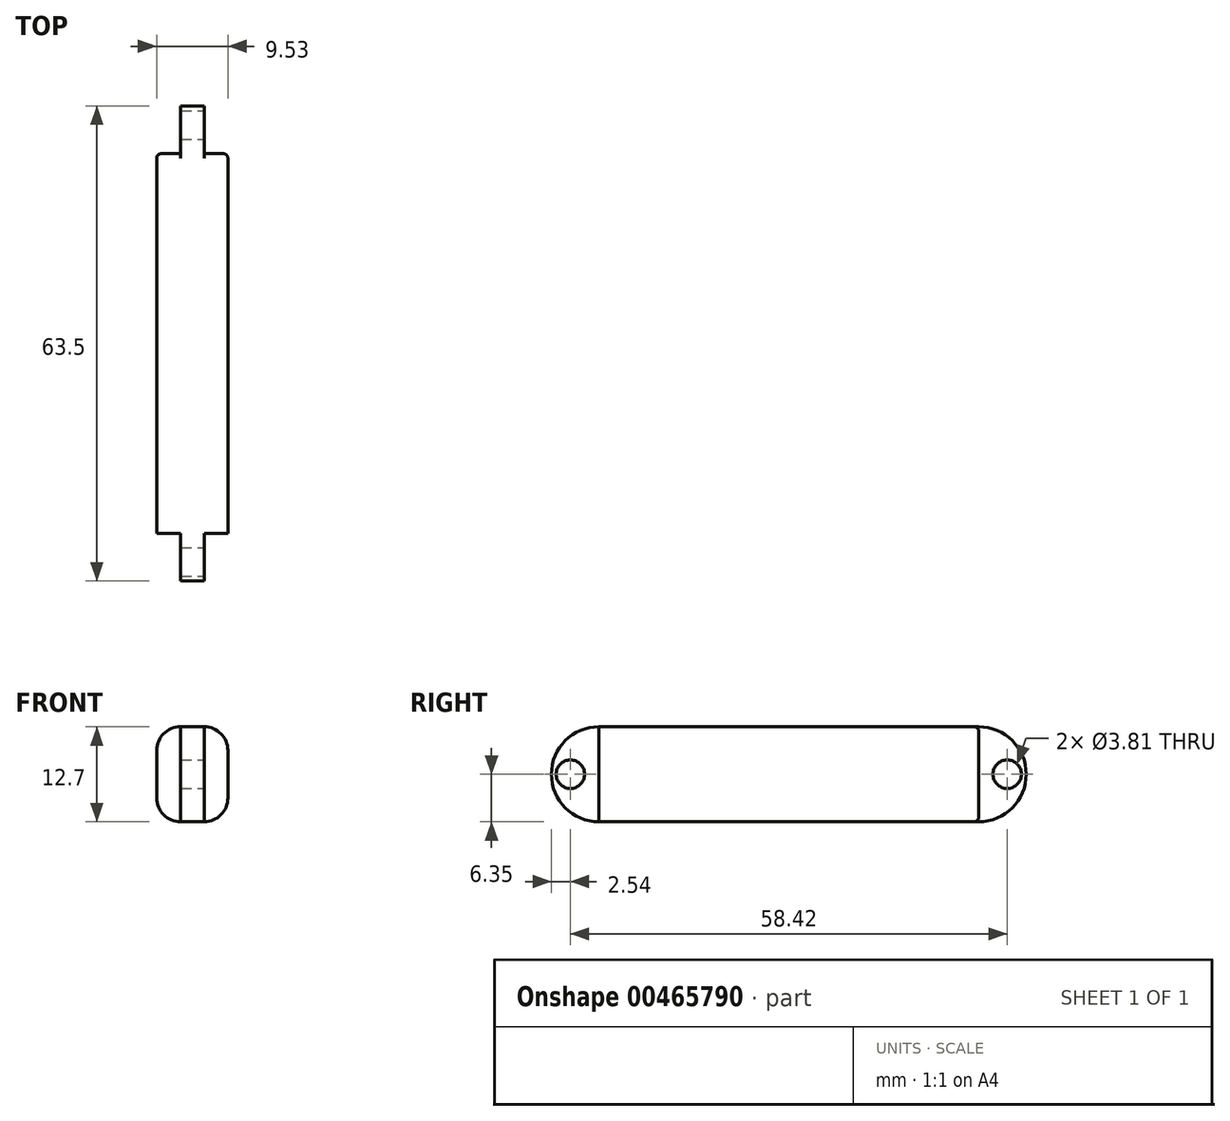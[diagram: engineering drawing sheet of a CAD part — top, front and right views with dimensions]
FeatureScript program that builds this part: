
annotation { "Feature Type Name" : "Feature", "Feature Type Description" : "" }
export const myFeature = defineFeature(function(context is Context, id is Id, definition is map)
    precondition{}
    {
        {
            var Q0;
            Q0=qCreatedBy(makeId("Right.planeOp"),FACE);
            var sketch = newSketch(context, id + "F0", { "sketchPlane" : qUnion([Q0])});
            skLineSegment(sketch, "E0.bottom", {"start": v(0, 0) * mm, "end": v(50.8, 0) * mm});
            skLineSegment(sketch, "E0.top", {"start": v(0, 12.7) * mm, "end": v(50.8, 12.7) * mm});
            skLineSegment(sketch, "E0.left", {"start": v(0, 0) * mm, "end": v(0, 12.7) * mm});
            skLineSegment(sketch, "E0.right", {"start": v(50.8, 0) * mm, "end": v(50.8, 12.7) * mm});
            skSolve(sketch);
        }
        {
            var Q0;
            Q0=qSketchRegion(id+"F0",true);
            extrude(context, id + "F1", {"entities" : qUnion([Q0]), "depth" : 9.52 * mm});
        }
        {
            var Q0;
            Q0=makeQuery(id+"F1.opExtrude","CAP_FACE",FACE,{"disambiguationData":[OSD([sQuery(id+"F0.wireOp",EDGE,"E0.bottom"),sQuery(id+"F0.wireOp",EDGE,"E0.top"),sQuery(id+"F0.wireOp",EDGE,"E0.left"),sQuery(id+"F0.wireOp",EDGE,"E0.right")])],"isStart":true});
            var sketch = newSketch(context, id + "F2", { "sketchPlane" : qUnion([Q0])});
            skArc(sketch, "E1", {"start": v(0, 12.7) * mm, "mid": v(6.35, 6.35) * mm, "end": v(0, 0) * mm});
            skArc(sketch, "E2", {"start": v(-50.8, 0) * mm, "mid": v(-57.15, 6.35) * mm, "end": v(-50.8, 12.7) * mm});
            skLineSegment(sketch, "E3", {"start": v(0, 0) * mm, "end": v(0, 12.7) * mm});
            skLineSegment(sketch, "E4", {"start": v(-50.8, 0) * mm, "end": v(-50.8, 12.7) * mm});
            skSolve(sketch);
        }
        {
            var Q0;
            Q0=qSketchRegion(id+"F2",true);
            var Q1;
            Q1=makeQuery(id+"F2.imprint","IMPRINT",FACE,{"disambiguationData":[TD([[makeQuery(id+"F2.imprint","IMPRINT",EDGE,{"derivedFrom":sQuery(id+"F2.wireOp",EDGE,"E2")}),-1.0]])]});
            var Q2;
            Q2=makeQuery(id+"F2.imprint","IMPRINT",FACE,{"disambiguationData":[TD([[makeQuery(id+"F2.imprint","IMPRINT",EDGE,{"derivedFrom":sQuery(id+"F2.wireOp",EDGE,"E1")}),-1.0]])]});
            extrude(context, id + "F3", {"entities" : qUnion([Q0, Q1, Q2]), "operationType" : NewBodyOperationType.ADD, "oppositeDirection" : true, "depth" : 9.52 * mm});
        }
        {
            var Q0;
            Q0=qSketchRegion(id+"F2",true);
            extrude(context, id + "F4", {"entities" : qUnion([Q0]), "operationType" : NewBodyOperationType.REMOVE, "oppositeDirection" : true, "depth" : 3.17 * mm});
        }
        {
            var Q0;
            Q0=makeQuery(id+"F3.boolean.opBoolean","MERGE",FACE,{"derivedFrom":[makeQuery(id+"F1.opExtrude","CAP_FACE",FACE,{"disambiguationData":[OSD([sQuery(id+"F0.wireOp",EDGE,"E0.bottom"),sQuery(id+"F0.wireOp",EDGE,"E0.top"),sQuery(id+"F0.wireOp",EDGE,"E0.left"),sQuery(id+"F0.wireOp",EDGE,"E0.right")])],"isStart":false}),makeQuery(id+"F3.opExtrude","CAP_FACE",FACE,{"disambiguationData":[OSD([sQuery(id+"F2.wireOp",EDGE,"E1"),sQuery(id+"F2.wireOp",EDGE,"E3")])],"isStart":false}),makeQuery(id+"F3.opExtrude","CAP_FACE",FACE,{"disambiguationData":[OSD([sQuery(id+"F2.wireOp",EDGE,"E2"),sQuery(id+"F2.wireOp",EDGE,"E4")])],"isStart":false})]});
            var sketch = newSketch(context, id + "F5", { "sketchPlane" : qUnion([Q0])});
            skLineSegment(sketch, "E5", {"start": v(0, 0) * mm, "end": v(0, 12.7) * mm});
            skLineSegment(sketch, "E6", {"start": v(0, 12.7) * mm, "end": v(50.8, 12.7) * mm});
            skLineSegment(sketch, "E7", {"start": v(50.8, 12.7) * mm, "end": v(50.8, 0) * mm});
            skLineSegment(sketch, "E8", {"start": v(50.8, 0) * mm, "end": v(0, 0) * mm});
            skLineSegment(sketch, "E9", {"start": v(50.8, 6.35) * mm, "end": v(54.61, 6.35) * mm});
            skPoint(sketch, "E9.endSnap0", {"position": v(50.8, 6.35) * mm});
            skLineSegment(sketch, "E10", {"start": v(0, 6.35) * mm, "end": v(-3.81, 6.35) * mm});
            skCircle(sketch, "E11", {"center": v(-3.81, 6.35) * mm, "radius": 1.9 * mm});
            skCircle(sketch, "E12", {"center": v(54.61, 6.35) * mm, "radius": 1.9 * mm});
            skSolve(sketch);
        }
        {
            var Q0;
            Q0=makeQuery(id+"F5.imprint","IMPRINT",FACE,{"disambiguationData":[TD([[makeQuery(id+"F5.imprint","IMPRINT",EDGE,{"derivedFrom":sQuery(id+"F5.wireOp",EDGE,"E5")}),1.0]])]});
            var Q1;
            Q1=makeQuery(id+"F5.imprint","IMPRINT",FACE,{"disambiguationData":[TD([[makeQuery(id+"F5.imprint","IMPRINT",EDGE,{"derivedFrom":sQuery(id+"F5.wireOp",EDGE,"E7")}),1.0]])]});
            extrude(context, id + "F6", {"entities" : qUnion([Q0, Q1]), "operationType" : NewBodyOperationType.REMOVE, "oppositeDirection" : true, "depth" : 3.17 * mm});
        }
        {
            var Q0;
            Q0=makeQuery(id+"F1.opExtrude","CAP_EDGE",EDGE,{"disambiguationData":[OSD([sQuery(id+"F0.wireOp",EDGE,"E0.top")])],"isStart":true});
            var Q1;
            Q1=makeQuery(id+"F1.opExtrude","CAP_EDGE",EDGE,{"disambiguationData":[OSD([sQuery(id+"F0.wireOp",EDGE,"E0.top")])],"isStart":false});
            var Q2;
            Q2=makeQuery(id+"F1.opExtrude","CAP_EDGE",EDGE,{"disambiguationData":[OSD([sQuery(id+"F0.wireOp",EDGE,"E0.bottom")])],"isStart":false});
            var Q3;
            Q3=makeQuery(id+"F1.opExtrude","CAP_EDGE",EDGE,{"disambiguationData":[OSD([sQuery(id+"F0.wireOp",EDGE,"E0.bottom")])],"isStart":true});
            fillet(context, id + "F7", {"entities" : qUnion([Q0, Q1, Q2, Q3]), "radius" : 3.17 * mm, "tangentPropagation" : true, "allowEdgeOverflow" : false});
        }
        {
            var Q0;
            Q0=makeQuery(id+"F6.boolean.opBoolean","COPY",EDGE,{"derivedFrom":makeQuery(id+"F6.opExtrude","CAP_EDGE",EDGE,{"disambiguationData":[OSD([sQuery(id+"F2.wireOp",EDGE,"E1")])],"isStart":false})});
            var Q1;
            Q1=makeQuery(id+"F4.boolean.opBoolean","COPY",EDGE,{"derivedFrom":makeQuery(id+"F4.opExtrude","CAP_EDGE",EDGE,{"disambiguationData":[OSD([sQuery(id+"F2.wireOp",EDGE,"E1")])],"isStart":false})});
            var Q2;
            Q2=makeQuery(id+"F6.boolean.opBoolean","COPY",EDGE,{"derivedFrom":makeQuery(id+"F6.opExtrude","CAP_EDGE",EDGE,{"disambiguationData":[OSD([sQuery(id+"F2.wireOp",EDGE,"E2")])],"isStart":false})});
            var Q3;
            Q3=makeQuery(id+"F4.boolean.opBoolean","COPY",EDGE,{"derivedFrom":makeQuery(id+"F4.opExtrude","CAP_EDGE",EDGE,{"disambiguationData":[OSD([sQuery(id+"F2.wireOp",EDGE,"E2")])],"isStart":false})});
            var Q4;
            Q4=makeQuery(id+"F7.opFillet","BLEND_EDGE",EDGE,{"blendedFrom":[makeQuery(id+"F1.opExtrude","CAP_EDGE",EDGE,{"disambiguationData":[OSD([sQuery(id+"F0.wireOp",EDGE,"E0.bottom")])],"isStart":true}),makeQuery(id+"F4.boolean.opBoolean","COPY",FACE,{"derivedFrom":makeQuery(id+"F4.opExtrude","SWEPT_FACE",FACE,{"disambiguationData":[OSD([sQuery(id+"F2.wireOp",EDGE,"E4")])]})})],"blendedInto":[makeQuery(id+"F4.boolean.opBoolean","COPY",FACE,{"derivedFrom":makeQuery(id+"F4.opExtrude","SWEPT_FACE",FACE,{"disambiguationData":[OSD([sQuery(id+"F2.wireOp",EDGE,"E4")])]})})]});
            var Q5;
            Q5=makeQuery(id+"F6.boolean.opBoolean","COPY",EDGE,{"derivedFrom":makeQuery(id+"F6.opExtrude","CAP_EDGE",EDGE,{"disambiguationData":[OSD([sQuery(id+"F5.wireOp",EDGE,"E7")])],"isStart":true})});
            var Q6;
            Q6=makeQuery(id+"F4.boolean.opBoolean","COPY",EDGE,{"derivedFrom":makeQuery(id+"F4.opExtrude","CAP_EDGE",EDGE,{"disambiguationData":[OSD([sQuery(id+"F2.wireOp",EDGE,"E3")])],"isStart":true})});
            var Q7;
            Q7=makeQuery(id+"F6.boolean.opBoolean","COPY",EDGE,{"derivedFrom":makeQuery(id+"F6.opExtrude","CAP_EDGE",EDGE,{"disambiguationData":[OSD([sQuery(id+"F5.wireOp",EDGE,"E5")])],"isStart":true})});
            fillet(context, id + "F8", {"entities" : qUnion([Q0, Q1, Q2, Q3, Q4, Q5, Q6, Q7]), "radius" : 0.64 * mm, "tangentPropagation" : true, "allowEdgeOverflow" : false});
        }
        {
            var Q0;
            Q0=makeQuery(id+"F6.boolean.opBoolean","SPLIT",FACE,{"disambiguationData":[TD([makeQuery(id+"F6.opExtrude","SWEPT_FACE",FACE,{"disambiguationData":[OSD([sQuery(id+"F5.wireOp",EDGE,"E12")])]})])],"derivedFrom":makeQuery(id+"F3.boolean.opBoolean","MERGE",FACE,{"derivedFrom":[makeQuery(id+"F1.opExtrude","CAP_FACE",FACE,{"disambiguationData":[OSD([sQuery(id+"F0.wireOp",EDGE,"E0.bottom"),sQuery(id+"F0.wireOp",EDGE,"E0.top"),sQuery(id+"F0.wireOp",EDGE,"E0.left"),sQuery(id+"F0.wireOp",EDGE,"E0.right")])],"isStart":false}),makeQuery(id+"F3.opExtrude","CAP_FACE",FACE,{"disambiguationData":[OSD([sQuery(id+"F2.wireOp",EDGE,"E1"),sQuery(id+"F2.wireOp",EDGE,"E3")])],"isStart":false}),makeQuery(id+"F3.opExtrude","CAP_FACE",FACE,{"disambiguationData":[OSD([sQuery(id+"F2.wireOp",EDGE,"E2"),sQuery(id+"F2.wireOp",EDGE,"E4")])],"isStart":false})]})});
            var Q1;
            Q1=makeQuery(id+"F6.boolean.opBoolean","SPLIT",FACE,{"disambiguationData":[TD([makeQuery(id+"F6.opExtrude","SWEPT_FACE",FACE,{"disambiguationData":[OSD([sQuery(id+"F5.wireOp",EDGE,"E11")])]})])],"derivedFrom":makeQuery(id+"F3.boolean.opBoolean","MERGE",FACE,{"derivedFrom":[makeQuery(id+"F1.opExtrude","CAP_FACE",FACE,{"disambiguationData":[OSD([sQuery(id+"F0.wireOp",EDGE,"E0.bottom"),sQuery(id+"F0.wireOp",EDGE,"E0.top"),sQuery(id+"F0.wireOp",EDGE,"E0.left"),sQuery(id+"F0.wireOp",EDGE,"E0.right")])],"isStart":false}),makeQuery(id+"F3.opExtrude","CAP_FACE",FACE,{"disambiguationData":[OSD([sQuery(id+"F2.wireOp",EDGE,"E1"),sQuery(id+"F2.wireOp",EDGE,"E3")])],"isStart":false}),makeQuery(id+"F3.opExtrude","CAP_FACE",FACE,{"disambiguationData":[OSD([sQuery(id+"F2.wireOp",EDGE,"E2"),sQuery(id+"F2.wireOp",EDGE,"E4")])],"isStart":false})]})});
            extrude(context, id + "F9", {"entities" : qUnion([Q0, Q1]), "operationType" : NewBodyOperationType.REMOVE, "oppositeDirection" : true, "depth" : 25.4 * mm});
        }
    });
